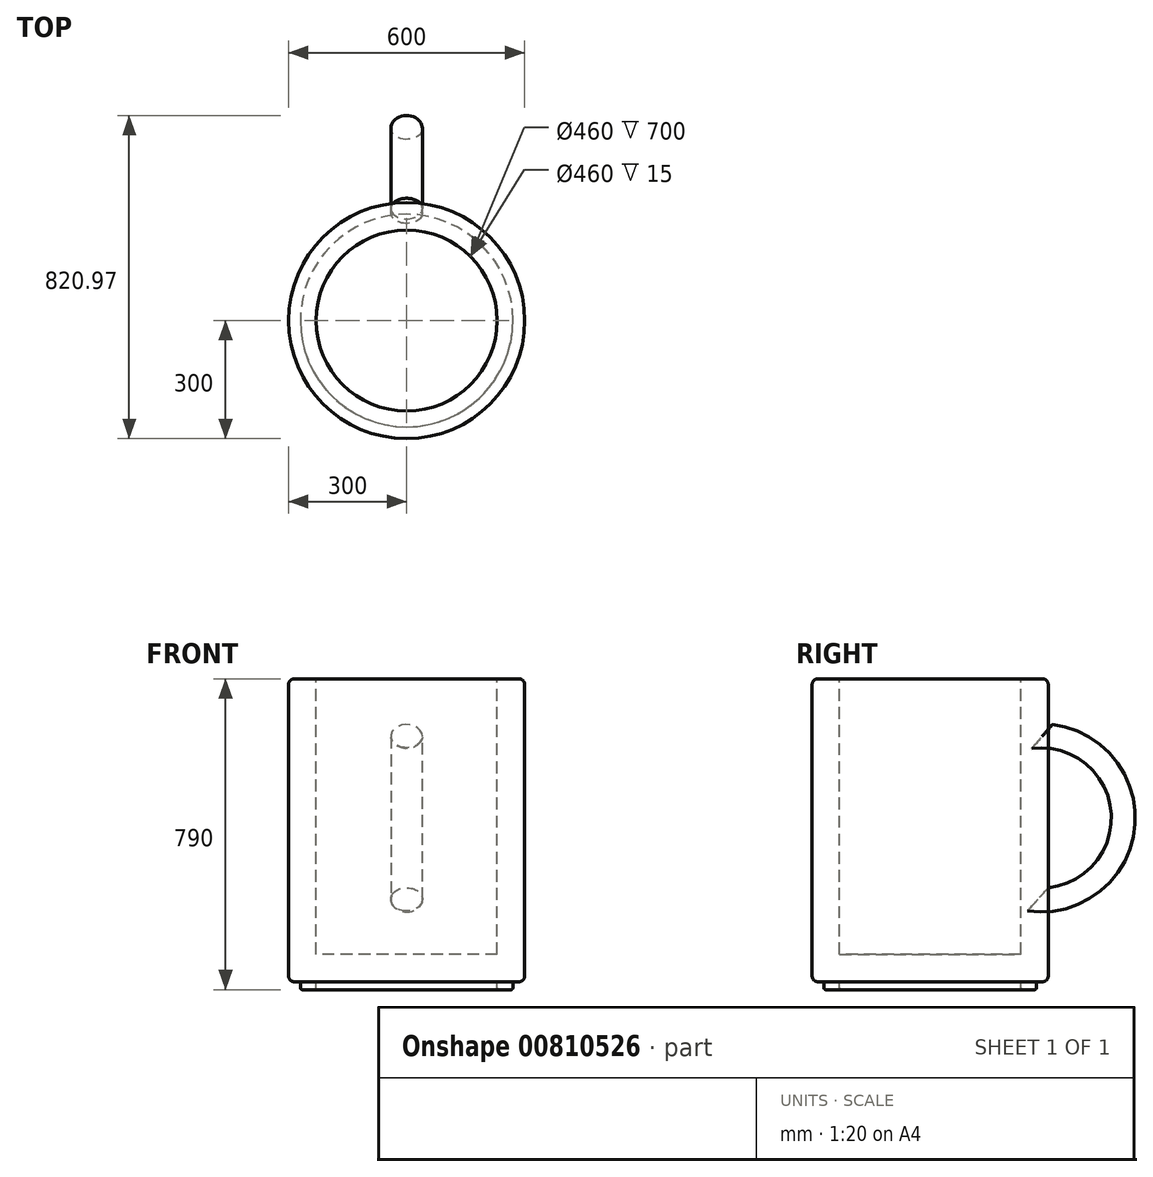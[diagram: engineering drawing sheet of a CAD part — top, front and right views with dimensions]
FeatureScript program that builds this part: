
annotation { "Feature Type Name" : "Feature", "Feature Type Description" : "" }
export const myFeature = defineFeature(function(context is Context, id is Id, definition is map)
    precondition{}
    {
        {
            var Q0;
            Q0=qCreatedBy(makeId("Top.planeOp"),FACE);
            var sketch = newSketch(context, id + "F0", { "sketchPlane" : qUnion([Q0])});
            skCircle(sketch, "E0", {"center": v(0, 0) * mm, "radius": 300 * mm});
            skSolve(sketch);
        }
        {
            var Q0;
            Q0=makeQuery(id+"F0.imprint","IMPRINT",FACE,{"disambiguationData":[TD([[makeQuery(id+"F0.imprint","IMPRINT",EDGE,{"derivedFrom":sQuery(id+"F0.wireOp",EDGE,"E0")}),1.0]])]});
            extrude(context, id + "F1", {"entities" : qUnion([Q0]), "depth" : 770 * mm, "offsetDistance" : 25 * mm});
        }
        {
            var Q0;
            Q0=makeQuery(id+"F1.opExtrude","CAP_FACE",FACE,{"disambiguationData":[OSD([sQuery(id+"F0.wireOp",EDGE,"E0")])],"isStart":false});
            var sketch = newSketch(context, id + "F2", { "sketchPlane" : qUnion([Q0])});
            skCircle(sketch, "E1", {"center": v(0, 0) * mm, "radius": 230 * mm});
            skSolve(sketch);
        }
        {
            var Q0;
            Q0=makeQuery(id+"F2.imprint","IMPRINT",FACE,{"disambiguationData":[TD([[makeQuery(id+"F2.imprint","IMPRINT",EDGE,{"derivedFrom":sQuery(id+"F2.wireOp",EDGE,"E1")}),1.0]])]});
            extrude(context, id + "F3", {"entities" : qUnion([Q0]), "operationType" : NewBodyOperationType.REMOVE, "oppositeDirection" : true, "depth" : 700 * mm, "offsetDistance" : 25 * mm});
        }
        {
            var Q0;
            Q0=makeQuery(id+"F1.opExtrude","CAP_EDGE",EDGE,{"disambiguationData":[OSD([sQuery(id+"F0.wireOp",EDGE,"E0")])],"isStart":false});
            var Q1;
            Q1=makeQuery(id+"F3.boolean.opBoolean","COPY",EDGE,{"derivedFrom":makeQuery(id+"F3.opExtrude","CAP_EDGE",EDGE,{"disambiguationData":[OSD([sQuery(id+"F2.wireOp",EDGE,"E1")])],"isStart":true})});
            var Q2;
            Q2=makeQuery(id+"F1.opExtrude","CAP_EDGE",EDGE,{"disambiguationData":[OSD([sQuery(id+"F0.wireOp",EDGE,"E0")])],"isStart":true});
            fillet(context, id + "F4", {"entities" : qUnion([Q0, Q1, Q2]), "radius" : 15 * mm, "tangentPropagation" : true, "allowEdgeOverflow" : false});
        }
        {
            var Q0;
            Q0=makeQuery(id+"F1.opExtrude","CAP_FACE",FACE,{"disambiguationData":[OSD([sQuery(id+"F0.wireOp",EDGE,"E0")])],"isStart":true});
            var sketch = newSketch(context, id + "F5", { "sketchPlane" : qUnion([Q0])});
            skCircle(sketch, "E2", {"center": v(0, 0) * mm, "radius": 270 * mm});
            skCircle(sketch, "E3", {"center": v(0, 0) * mm, "radius": 230 * mm});
            skSolve(sketch);
        }
        {
            var Q0;
            Q0=makeQuery(id+"F5.imprint","IMPRINT",FACE,{"disambiguationData":[TD([[makeQuery(id+"F5.imprint","IMPRINT",EDGE,{"derivedFrom":sQuery(id+"F5.wireOp",EDGE,"E2")}),1.0]])]});
            extrude(context, id + "F6", {"entities" : qUnion([Q0]), "operationType" : NewBodyOperationType.ADD, "depth" : 20 * mm, "offsetDistance" : 25 * mm});
        }
        {
            var Q0;
            Q0=makeQuery(id+"F6.opExtrude","CAP_EDGE",EDGE,{"disambiguationData":[OSD([sQuery(id+"F5.wireOp",EDGE,"E2")])],"isStart":false});
            var Q1;
            Q1=makeQuery(id+"F6.opExtrude","CAP_EDGE",EDGE,{"disambiguationData":[OSD([sQuery(id+"F5.wireOp",EDGE,"E3")])],"isStart":false});
            fillet(context, id + "F7", {"entities" : qUnion([Q0, Q1]), "radius" : 5 * mm, "tangentPropagation" : true, "allowEdgeOverflow" : false});
        }
        {
            var Q0;
            Q0=qCreatedBy(makeId("Front.planeOp"),FACE);
            cPlane(context, id + "F8", {"entities" : qUnion([Q0]), "cplaneType" : CPlaneType.OFFSET, "offset" : 280 * mm, "oppositeDirection" : true, "width" : 150 * mm, "height" : 150 * mm});
        }
        {
            var Q0;
            Q0=makeQuery(id+"F1.opExtrude","CAP_FACE",FACE,{"disambiguationData":[OSD([sQuery(id+"F0.wireOp",EDGE,"E0")])],"isStart":false});
            cPlane(context, id + "F9", {"entities" : qUnion([Q0]), "cplaneType" : CPlaneType.OFFSET, "offset" : 220 * mm, "oppositeDirection" : true, "width" : 150 * mm, "height" : 150 * mm});
        }
        {
            var Q0;
            Q0=qCreatedBy(id+"F9.planeOp",FACE);
            var sketch = newSketch(context, id + "F10", { "sketchPlane" : qUnion([Q0])});
            skLineSegment(sketch, "E4", {"start": v(0, 480.19) * mm, "end": v(0, 480.17) * mm});
            skCircle(sketch, "E5", {"center": v(0, 440.17) * mm, "radius": 40 * mm});
            skSolve(sketch);
        }
        {
            var Q0;
            Q0=qCreatedBy(makeId("Right.planeOp"),FACE);
            var sketch = newSketch(context, id + "F11", { "sketchPlane" : qUnion([Q0])});
            skArc(sketch, "E6", {"start": v(280.04, 216.43) * mm, "mid": v(481.93, 417.28) * mm, "end": v(278.34, 616.4) * mm});
            skSolve(sketch);
        }
        {
            var Q0;
            Q0=makeQuery(id+"F10.imprint","IMPRINT",FACE,{"disambiguationData":[TD([[makeQuery(id+"F10.imprint","IMPRINT",EDGE,{"derivedFrom":sQuery(id+"F10.wireOp",EDGE,"E5")}),1.0]])]});
            var Q1;
            Q1=sQuery(id+"F11.wireOp",EDGE,"E6");
            sweep(context, id + "F12", {"profiles" : qUnion([Q0]), "path" : qUnion([Q1])});
        }
    });
